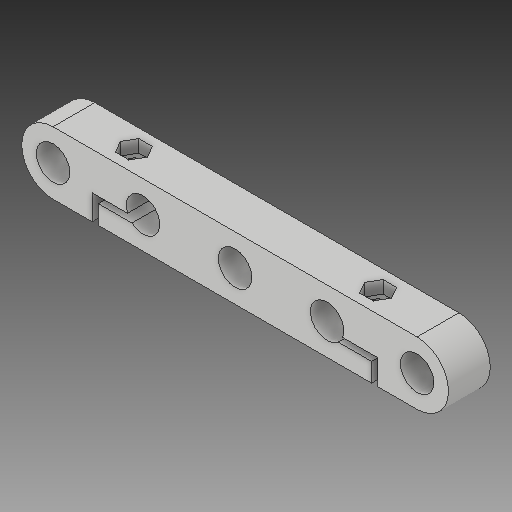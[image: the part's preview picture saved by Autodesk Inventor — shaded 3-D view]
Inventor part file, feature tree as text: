
AUTODESK INVENTOR PART (.ipt)
format: ipt  version: 2017 SP1 (Build 210196100, 196)  size: 186,368 bytes
history: native  units: mm
features: extrude x4, sketch x4, mirror x1, projected_geometry x1
ambient origin geometry x8: Origin, YZ Plane, XZ Plane, XY Plane, X Axis, Y Axis, Z Axis, Center Point
bodies: Solid1 (feature_tree)
feature tree (10):
  extrude  "Extrusion1"  Depth=8.0mm
  extrude  "Extrusion2"  Depth=10.0mm TaperAngle=0.0deg
  extrude  "Extrusion3"  Depth=1.5mm
  extrude  "Extrusion4"  Depth=10.0mm TaperAngle=0.0deg
  mirror  "Mirror1"
  sketch  "Sketch1"  dims[d1=8.0mm d2=8.0mm]
  sketch  "Sketch2"  dims[d4=15.0mm d5=10.0mm d6=0.0mm]
  sketch  "Sketch3"  dims[d7=1.5mm d8=8.0mm]
  projected_geometry  "Projected Loop1"
  sketch  "Sketch4"  dims[d9=1.5mm d10=10.0mm d11=0.0mm d12=3.5mm d13=10.0mm d14=0.0mm d15=5.6mm d16=3.0mm d17=0.0mm d18=1.0mm d19=43.5mm d22=22.0mm]
